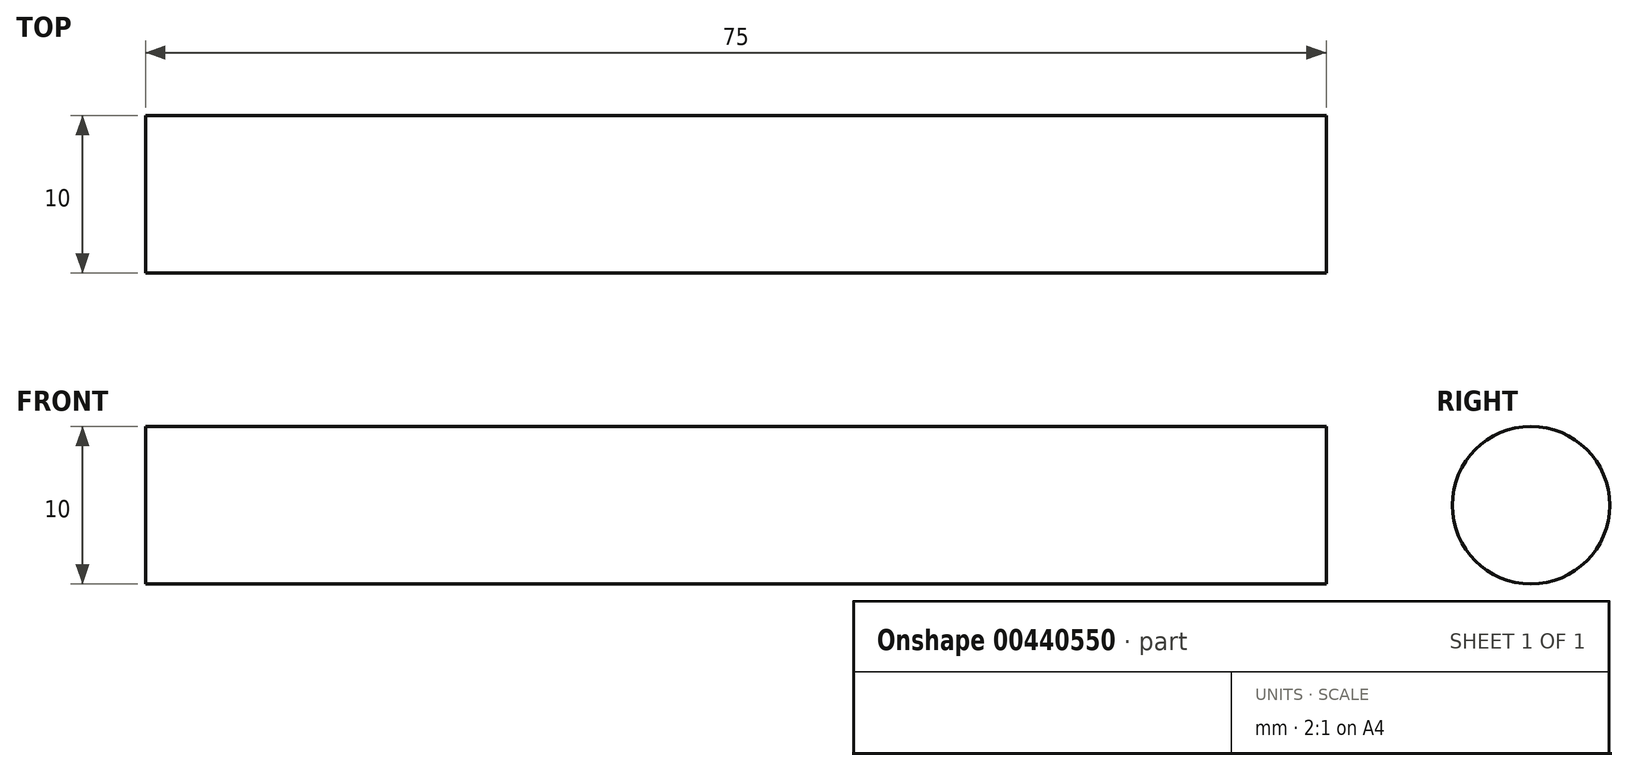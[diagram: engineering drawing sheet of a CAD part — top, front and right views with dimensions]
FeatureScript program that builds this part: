
annotation { "Feature Type Name" : "Feature", "Feature Type Description" : "" }
export const myFeature = defineFeature(function(context is Context, id is Id, definition is map)
    precondition{}
    {
        {
            var Q0;
            Q0=qCreatedBy(makeId("Top.planeOp"),FACE);
            var sketch = newSketch(context, id + "F0", { "sketchPlane" : qUnion([Q0])});
            skLineSegment(sketch, "E0", {"start": v(0, 0) * mm, "end": v(75, 0) * mm});
            skLineSegment(sketch, "E1", {"start": v(0, 0) * mm, "end": v(0, 5) * mm});
            skLineSegment(sketch, "E2", {"start": v(0, 5) * mm, "end": v(75, 5) * mm});
            skLineSegment(sketch, "E3", {"start": v(75, 5) * mm, "end": v(75, 0) * mm});
            skLineSegment(sketch, "E4.MirrorCS", {"start": v(0, -5) * mm, "end": v(75, -5) * mm});
            skLineSegment(sketch, "E5.MirrorCS", {"start": v(0, 0) * mm, "end": v(0, -5) * mm});
            skLineSegment(sketch, "E6.MirrorCS", {"start": v(75, -5) * mm, "end": v(75, 0) * mm});
            skSolve(sketch);
        }
        {
            var Q0;
            Q0=makeQuery(id+"F0.imprint","IMPRINT",FACE,{"disambiguationData":[TD([[makeQuery(id+"F0.imprint","IMPRINT",EDGE,{"derivedFrom":sQuery(id+"F0.wireOp",EDGE,"E0")}),1.0]])]});
            var Q1;
            Q1=sQuery(id+"F0.wireOp",EDGE,"E0");
            revolve(context, id + "F1", {"entities" : qUnion([Q0]), "axis" : qUnion([Q1]), "revolveType" : RevolveType.FULL});
        }
    });
